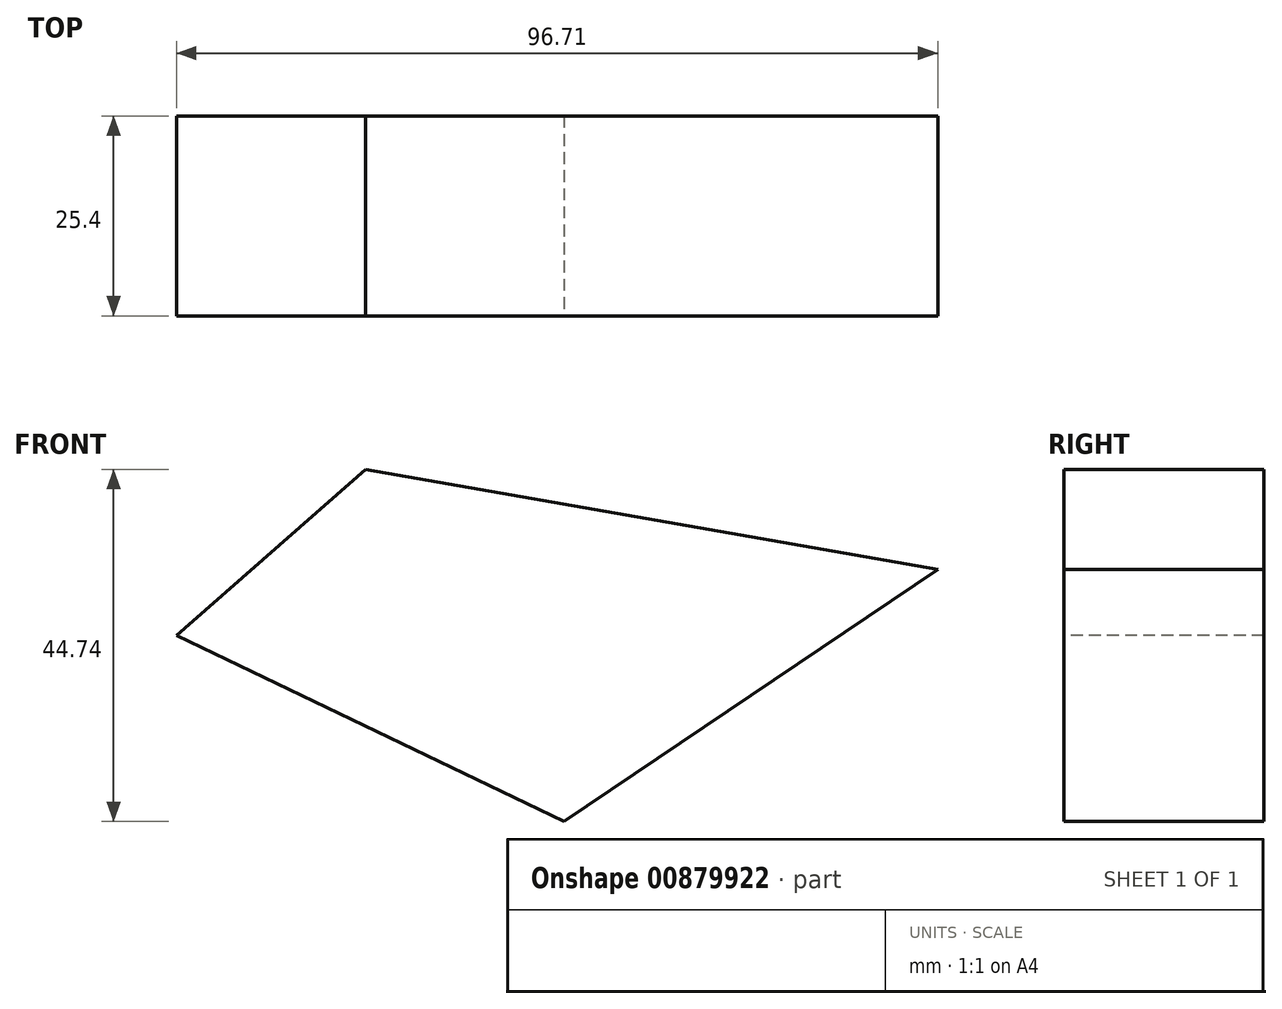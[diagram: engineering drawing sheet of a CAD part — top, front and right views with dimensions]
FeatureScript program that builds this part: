
annotation { "Feature Type Name" : "Feature", "Feature Type Description" : "" }
export const myFeature = defineFeature(function(context is Context, id is Id, definition is map)
    precondition{}
    {
        {
            var Q0;
            Q0=qCreatedBy(makeId("Front.planeOp"),FACE);
            var sketch = newSketch(context, id + "F0", { "sketchPlane" : qUnion([Q0])});
            skLineSegment(sketch, "E0", {"start": v(-45.62, 29.11) * mm, "end": v(27.06, 16.41) * mm});
            skLineSegment(sketch, "E1", {"start": v(27.06, 16.41) * mm, "end": v(-20.42, -15.63) * mm});
            skLineSegment(sketch, "E2", {"start": v(-20.42, -15.63) * mm, "end": v(-69.65, 8.01) * mm});
            skLineSegment(sketch, "E3", {"start": v(-69.65, 8.01) * mm, "end": v(-45.62, 29.11) * mm});
            skSolve(sketch);
        }
        {
            var Q0;
            Q0=makeQuery(id+"F0.imprint","IMPRINT",FACE,{"disambiguationData":[TD([[makeQuery(id+"F0.imprint","IMPRINT",EDGE,{"derivedFrom":sQuery(id+"F0.wireOp",EDGE,"E0")}),-1.0]])]});
            var Q1;
            Q1=sQuery(id+"F0.wireOp",EDGE,"E0");
            var Q2;
            Q2=sQuery(id+"F0.wireOp",EDGE,"E2");
            var Q3;
            Q3=sQuery(id+"F0.wireOp",EDGE,"E3");
            var Q4;
            Q4=sQuery(id+"F0.wireOp",EDGE,"E1");
            extrude(context, id + "F1", {"entities" : qUnion([Q0]), "bodyType" : ToolBodyType.SURFACE, "surfaceEntities" : qUnion([Q1, Q2, Q3, Q4]), "depth" : 25.4 * mm, "offsetDistance" : 25.4 * mm});
        }
    });
